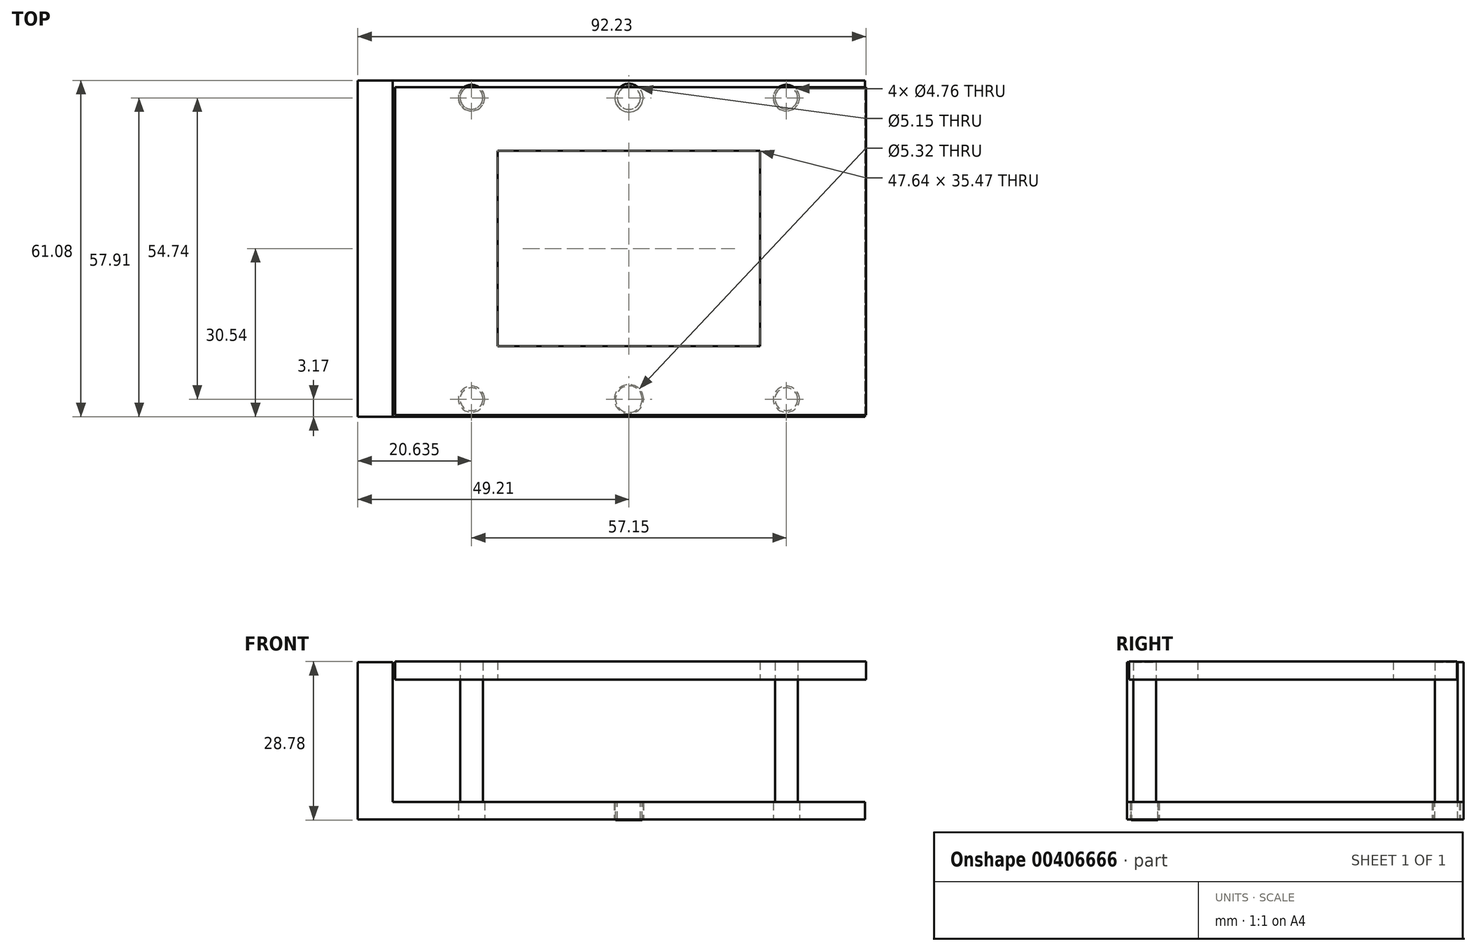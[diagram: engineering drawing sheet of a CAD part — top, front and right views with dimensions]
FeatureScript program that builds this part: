
annotation { "Feature Type Name" : "Feature", "Feature Type Description" : "" }
export const myFeature = defineFeature(function(context is Context, id is Id, definition is map)
    precondition{}
    {
        {
            var Q0;
            Q0=qCreatedBy(makeId("Top.planeOp"),FACE);
            var sketch = newSketch(context, id + "F0", { "sketchPlane" : qUnion([Q0])});
            skLineSegment(sketch, "E0.bottom", {"start": v(42.86, -24.2) * mm, "end": v(-42.86, -24.2) * mm});
            skLineSegment(sketch, "E0.top", {"start": v(42.86, 24.2) * mm, "end": v(-42.86, 24.2) * mm});
            skLineSegment(sketch, "E0.left", {"start": v(42.86, -24.2) * mm, "end": v(42.86, 24.2) * mm});
            skLineSegment(sketch, "E0.right", {"start": v(-42.86, -24.2) * mm, "end": v(-42.86, 24.2) * mm});
            skPoint(sketch, "E0.middle", {"position": v(0, 0) * mm});
            skPoint(sketch, "E1.startSnap0", {"position": v(0, -24.2) * mm});
            skPoint(sketch, "E2.left.start.orphan", {"position": v(49.21, -34.93) * mm});
            skPoint(sketch, "E2.top.start.orphan", {"position": v(49.21, 34.93) * mm});
            skPoint(sketch, "E2.right.end.orphan", {"position": v(-49.21, 34.93) * mm});
            skPoint(sketch, "E2.right.start.orphan", {"position": v(-49.21, -34.93) * mm});
            skCircle(sketch, "E3", {"center": v(28.57, 27.37) * mm, "radius": 2.38 * mm});
            skCircle(sketch, "E4", {"center": v(-28.58, 27.37) * mm, "radius": 2.38 * mm});
            skPoint(sketch, "E5.end.orphan", {"position": v(-37.08, 27.37) * mm});
            skCircle(sketch, "E6", {"center": v(-28.58, -27.37) * mm, "radius": 2.38 * mm});
            skPoint(sketch, "E7.start.orphan", {"position": v(-35.98, -24.2) * mm});
            skPoint(sketch, "E8.orphan", {"position": v(-35.98, -27.37) * mm});
            skPoint(sketch, "E9.orphan", {"position": v(-23.88, -27.37) * mm});
            skPoint(sketch, "E10.start.orphan", {"position": v(0, -12.55) * mm});
            skPoint(sketch, "E11.start.orphan", {"position": v(0, 16.89) * mm});
            skPoint(sketch, "E12.start.orphan", {"position": v(0, -17.21) * mm});
            skPoint(sketch, "E1.start.orphan", {"position": v(0, 12.3) * mm});
            skLineSegment(sketch, "E13", {"start": v(0, -24.2) * mm, "end": v(0, -30.54) * mm});
            skLineSegment(sketch, "E14", {"start": v(42.86, -24.2) * mm, "end": v(42.86, -30.54) * mm});
            skLineSegment(sketch, "E15", {"start": v(-42.86, -24.2) * mm, "end": v(-42.86, -30.54) * mm});
            skLineSegment(sketch, "E16", {"start": v(0, -30.54) * mm, "end": v(42.86, -30.54) * mm});
            skLineSegment(sketch, "E17", {"start": v(-42.86, -30.54) * mm, "end": v(0, -30.54) * mm});
            skLineSegment(sketch, "E18", {"start": v(-42.86, 0) * mm, "end": v(-49.21, 0) * mm});
            skPoint(sketch, "E18.endSnap0", {"position": v(-42.86, 0) * mm});
            skLineSegment(sketch, "E19", {"start": v(-49.21, 0) * mm, "end": v(-49.21, -30.54) * mm});
            skLineSegment(sketch, "E20", {"start": v(-49.21, 0) * mm, "end": v(-49.21, 30.54) * mm});
            skLineSegment(sketch, "E21", {"start": v(-42.86, -30.54) * mm, "end": v(-49.21, -30.54) * mm});
            skPoint(sketch, "E22.endSnap0", {"position": v(0, 24.2) * mm});
            skLineSegment(sketch, "E23", {"start": v(42.86, 24.2) * mm, "end": v(42.86, 30.54) * mm});
            skLineSegment(sketch, "E24", {"start": v(0, 30.54) * mm, "end": v(42.86, 30.54) * mm});
            skLineSegment(sketch, "E25", {"start": v(0, 30.54) * mm, "end": v(-49.21, 30.54) * mm});
            skPoint(sketch, "E22.start.orphan", {"position": v(0, 24.2) * mm});
            skLineSegment(sketch, "E26", {"start": v(28.57, 27.37) * mm, "end": v(28.57, 3.32) * mm});
            skCircle(sketch, "E27", {"center": v(28.57, -27.37) * mm, "radius": 2.38 * mm});
            skLineSegment(sketch, "E28.bottom", {"start": v(4.2, -30.54) * mm, "end": v(-4.2, -30.54) * mm});
            skLineSegment(sketch, "E28.top", {"start": v(4.2, -24.2) * mm, "end": v(-4.2, -24.2) * mm});
            skPoint(sketch, "E28.middle", {"position": v(0, -27.37) * mm});
            skCircle(sketch, "E29", {"center": v(0, -27.37) * mm, "radius": 2.66 * mm});
            skCircle(sketch, "E30", {"center": v(0, 27.37) * mm, "radius": 2.57 * mm});
            skSolve(sketch);
        }
        {
            var Q0;
            Q0 = qSketchRegion(id + "F0", true);
            var Q1;
            {var subQ1=sQuery(id+"F0.wireOp",EDGE,"E15");Q1=makeQuery(id+"F0.imprint","IMPRINT",FACE,{"disambiguationData":[TD([[makeQuery(id+"F0.imprint","IMPRINT",EDGE,{"derivedFrom":subQ1}),-1.0]])]});}
            extrude(context, id + "F1", {"entities" : qUnion([Q0, Q1]), "depth" : 3.17 * mm, "offsetDistance" : 25.4 * mm});
        }
        {
            var Q0;
            Q0=makeQuery(id+"F1.opExtrude","CAP_FACE",FACE,{"disambiguationData":[OSD([sQuery(id+"F0.wireOp",EDGE,"E0.left"),sQuery(id+"F0.wireOp",EDGE,"E3"),sQuery(id+"F0.wireOp",EDGE,"E4"),sQuery(id+"F0.wireOp",EDGE,"E6"),sQuery(id+"F0.wireOp",EDGE,"E14"),sQuery(id+"F0.wireOp",EDGE,"E16"),sQuery(id+"F0.wireOp",EDGE,"E17"),sQuery(id+"F0.wireOp",EDGE,"E19"),sQuery(id+"F0.wireOp",EDGE,"E20"),sQuery(id+"F0.wireOp",EDGE,"E21"),sQuery(id+"F0.wireOp",EDGE,"E23"),sQuery(id+"F0.wireOp",EDGE,"E24"),sQuery(id+"F0.wireOp",EDGE,"E25"),sQuery(id+"F0.wireOp",EDGE,"E27"),sQuery(id+"F0.wireOp",EDGE,"E28.bottom"),sQuery(id+"F0.wireOp",EDGE,"E29"),sQuery(id+"F0.wireOp",EDGE,"E30")])],"isStart":false});
            var sketch = newSketch(context, id + "F2", { "sketchPlane" : qUnion([Q0])});
            skCircle(sketch, "E31", {"center": v(-28.58, 27.37) * mm, "radius": 2.06 * mm});
            skSolve(sketch);
        }
        {
            var Q0;
            Q0 = qSketchRegion(id + "F2", true);
            extrude(context, id + "F3", {"entities" : qUnion([Q0]), "depth" : 25.4 * mm, "offsetDistance" : 25.4 * mm});
        }
        {
            var Q0;
            Q0=makeQuery(id+"F1.opExtrude","CAP_FACE",FACE,{"disambiguationData":[OSD([sQuery(id+"F0.wireOp",EDGE,"E0.left"),sQuery(id+"F0.wireOp",EDGE,"E3"),sQuery(id+"F0.wireOp",EDGE,"E4"),sQuery(id+"F0.wireOp",EDGE,"E6"),sQuery(id+"F0.wireOp",EDGE,"E14"),sQuery(id+"F0.wireOp",EDGE,"E16"),sQuery(id+"F0.wireOp",EDGE,"E17"),sQuery(id+"F0.wireOp",EDGE,"E19"),sQuery(id+"F0.wireOp",EDGE,"E20"),sQuery(id+"F0.wireOp",EDGE,"E21"),sQuery(id+"F0.wireOp",EDGE,"E23"),sQuery(id+"F0.wireOp",EDGE,"E24"),sQuery(id+"F0.wireOp",EDGE,"E25"),sQuery(id+"F0.wireOp",EDGE,"E27"),sQuery(id+"F0.wireOp",EDGE,"E28.bottom"),sQuery(id+"F0.wireOp",EDGE,"E29"),sQuery(id+"F0.wireOp",EDGE,"E30")])],"isStart":false});
            var sketch = newSketch(context, id + "F4", { "sketchPlane" : qUnion([Q0])});
            skCircle(sketch, "E32", {"center": v(28.57, 27.37) * mm, "radius": 2.05 * mm});
            skSolve(sketch);
        }
        {
            var Q0;
            Q0 = qSketchRegion(id + "F4", true);
            extrude(context, id + "F5", {"entities" : qUnion([Q0]), "depth" : 25.4 * mm, "offsetDistance" : 25.4 * mm});
        }
        {
            var Q0;
            Q0=makeQuery(id+"F1.opExtrude","CAP_FACE",FACE,{"disambiguationData":[OSD([sQuery(id+"F0.wireOp",EDGE,"E0.left"),sQuery(id+"F0.wireOp",EDGE,"E3"),sQuery(id+"F0.wireOp",EDGE,"E4"),sQuery(id+"F0.wireOp",EDGE,"E6"),sQuery(id+"F0.wireOp",EDGE,"E14"),sQuery(id+"F0.wireOp",EDGE,"E16"),sQuery(id+"F0.wireOp",EDGE,"E17"),sQuery(id+"F0.wireOp",EDGE,"E19"),sQuery(id+"F0.wireOp",EDGE,"E20"),sQuery(id+"F0.wireOp",EDGE,"E21"),sQuery(id+"F0.wireOp",EDGE,"E23"),sQuery(id+"F0.wireOp",EDGE,"E24"),sQuery(id+"F0.wireOp",EDGE,"E25"),sQuery(id+"F0.wireOp",EDGE,"E27"),sQuery(id+"F0.wireOp",EDGE,"E28.bottom"),sQuery(id+"F0.wireOp",EDGE,"E29"),sQuery(id+"F0.wireOp",EDGE,"E30")])],"isStart":false});
            var sketch = newSketch(context, id + "F6", { "sketchPlane" : qUnion([Q0])});
            skCircle(sketch, "E33", {"center": v(-28.58, -27.37) * mm, "radius": 2.07 * mm});
            skSolve(sketch);
        }
        {
            var Q0;
            Q0 = qSketchRegion(id + "F6", true);
            extrude(context, id + "F7", {"entities" : qUnion([Q0]), "depth" : 25.4 * mm, "offsetDistance" : 25.4 * mm});
        }
        {
            var Q0;
            Q0=makeQuery(id+"F1.opExtrude","CAP_FACE",FACE,{"disambiguationData":[OSD([sQuery(id+"F0.wireOp",EDGE,"E0.left"),sQuery(id+"F0.wireOp",EDGE,"E3"),sQuery(id+"F0.wireOp",EDGE,"E4"),sQuery(id+"F0.wireOp",EDGE,"E6"),sQuery(id+"F0.wireOp",EDGE,"E14"),sQuery(id+"F0.wireOp",EDGE,"E16"),sQuery(id+"F0.wireOp",EDGE,"E17"),sQuery(id+"F0.wireOp",EDGE,"E19"),sQuery(id+"F0.wireOp",EDGE,"E20"),sQuery(id+"F0.wireOp",EDGE,"E21"),sQuery(id+"F0.wireOp",EDGE,"E23"),sQuery(id+"F0.wireOp",EDGE,"E24"),sQuery(id+"F0.wireOp",EDGE,"E25"),sQuery(id+"F0.wireOp",EDGE,"E27"),sQuery(id+"F0.wireOp",EDGE,"E28.bottom"),sQuery(id+"F0.wireOp",EDGE,"E29"),sQuery(id+"F0.wireOp",EDGE,"E30")])],"isStart":false});
            var sketch = newSketch(context, id + "F8", { "sketchPlane" : qUnion([Q0])});
            skCircle(sketch, "E34", {"center": v(28.57, -27.37) * mm, "radius": 2.06 * mm});
            skSolve(sketch);
        }
        {
            var Q0;
            Q0 = qSketchRegion(id + "F8", true);
            extrude(context, id + "F9", {"entities" : qUnion([Q0]), "depth" : 25.4 * mm, "offsetDistance" : 25.4 * mm});
        }
        {
            var Q0;
            Q0=makeQuery(id+"F1.opExtrude","CAP_FACE",FACE,{"disambiguationData":[OSD([sQuery(id+"F0.wireOp",EDGE,"E0.left"),sQuery(id+"F0.wireOp",EDGE,"E3"),sQuery(id+"F0.wireOp",EDGE,"E4"),sQuery(id+"F0.wireOp",EDGE,"E6"),sQuery(id+"F0.wireOp",EDGE,"E14"),sQuery(id+"F0.wireOp",EDGE,"E16"),sQuery(id+"F0.wireOp",EDGE,"E17"),sQuery(id+"F0.wireOp",EDGE,"E19"),sQuery(id+"F0.wireOp",EDGE,"E20"),sQuery(id+"F0.wireOp",EDGE,"E21"),sQuery(id+"F0.wireOp",EDGE,"E23"),sQuery(id+"F0.wireOp",EDGE,"E24"),sQuery(id+"F0.wireOp",EDGE,"E25"),sQuery(id+"F0.wireOp",EDGE,"E27"),sQuery(id+"F0.wireOp",EDGE,"E28.bottom"),sQuery(id+"F0.wireOp",EDGE,"E29"),sQuery(id+"F0.wireOp",EDGE,"E30")])],"isStart":false});
            var sketch = newSketch(context, id + "F10", { "sketchPlane" : qUnion([Q0])});
            skCircle(sketch, "E35", {"center": v(0, 27.37) * mm, "radius": 2.09 * mm});
            skSolve(sketch);
        }
        {
            var Q0;
            Q0 = qSketchRegion(id + "F10", true);
            extrude(context, id + "F11", {"entities" : qUnion([Q0]), "oppositeDirection" : true, "depth" : 3.17 * mm, "offsetDistance" : 25.4 * mm});
        }
        {
            var Q0;
            Q0=makeQuery(id+"F1.opExtrude","CAP_FACE",FACE,{"disambiguationData":[OSD([sQuery(id+"F0.wireOp",EDGE,"E0.left"),sQuery(id+"F0.wireOp",EDGE,"E3"),sQuery(id+"F0.wireOp",EDGE,"E4"),sQuery(id+"F0.wireOp",EDGE,"E6"),sQuery(id+"F0.wireOp",EDGE,"E14"),sQuery(id+"F0.wireOp",EDGE,"E16"),sQuery(id+"F0.wireOp",EDGE,"E17"),sQuery(id+"F0.wireOp",EDGE,"E19"),sQuery(id+"F0.wireOp",EDGE,"E20"),sQuery(id+"F0.wireOp",EDGE,"E21"),sQuery(id+"F0.wireOp",EDGE,"E23"),sQuery(id+"F0.wireOp",EDGE,"E24"),sQuery(id+"F0.wireOp",EDGE,"E25"),sQuery(id+"F0.wireOp",EDGE,"E27"),sQuery(id+"F0.wireOp",EDGE,"E28.bottom"),sQuery(id+"F0.wireOp",EDGE,"E29"),sQuery(id+"F0.wireOp",EDGE,"E30")])],"isStart":false});
            var sketch = newSketch(context, id + "F12", { "sketchPlane" : qUnion([Q0])});
            skCircle(sketch, "E36", {"center": v(0, -27.37) * mm, "radius": 2.4 * mm});
            skSolve(sketch);
        }
        {
            var Q0;
            Q0 = qSketchRegion(id + "F12", true);
            extrude(context, id + "F13", {"entities" : qUnion([Q0]), "oppositeDirection" : true, "depth" : 3.25 * mm, "offsetDistance" : 25.4 * mm});
        }
        {
            var Q0;
            Q0=makeQuery(id+"F1.opExtrude","CAP_FACE",FACE,{"disambiguationData":[OSD([sQuery(id+"F0.wireOp",EDGE,"E0.left"),sQuery(id+"F0.wireOp",EDGE,"E3"),sQuery(id+"F0.wireOp",EDGE,"E4"),sQuery(id+"F0.wireOp",EDGE,"E6"),sQuery(id+"F0.wireOp",EDGE,"E14"),sQuery(id+"F0.wireOp",EDGE,"E16"),sQuery(id+"F0.wireOp",EDGE,"E17"),sQuery(id+"F0.wireOp",EDGE,"E19"),sQuery(id+"F0.wireOp",EDGE,"E20"),sQuery(id+"F0.wireOp",EDGE,"E21"),sQuery(id+"F0.wireOp",EDGE,"E23"),sQuery(id+"F0.wireOp",EDGE,"E24"),sQuery(id+"F0.wireOp",EDGE,"E25"),sQuery(id+"F0.wireOp",EDGE,"E27"),sQuery(id+"F0.wireOp",EDGE,"E28.bottom"),sQuery(id+"F0.wireOp",EDGE,"E29"),sQuery(id+"F0.wireOp",EDGE,"E30")])],"isStart":false});
            var sketch = newSketch(context, id + "F14", { "sketchPlane" : qUnion([Q0])});
            skLineSegment(sketch, "E37.bottom", {"start": v(-49.21, 30.54) * mm, "end": v(-42.86, 30.54) * mm});
            skLineSegment(sketch, "E37.top", {"start": v(-49.21, -30.54) * mm, "end": v(-42.86, -30.54) * mm});
            skLineSegment(sketch, "E37.left", {"start": v(-49.21, 30.54) * mm, "end": v(-49.21, -30.54) * mm});
            skLineSegment(sketch, "E37.right", {"start": v(-42.86, 30.54) * mm, "end": v(-42.86, -30.54) * mm});
            skSolve(sketch);
        }
        {
            var Q0;
            Q0 = qSketchRegion(id + "F14", true);
            extrude(context, id + "F15", {"entities" : qUnion([Q0]), "operationType" : NewBodyOperationType.ADD, "depth" : 25.4 * mm, "offsetDistance" : 25.4 * mm});
        }
        {
            var Q0;
            Q0=qCreatedBy(makeId("Top.planeOp"),FACE);
            cPlane(context, id + "F16", {"entities" : qUnion([Q0]), "cplaneType" : CPlaneType.OFFSET, "offset" : 25.4 * mm, "width" : 152.4 * mm, "height" : 152.4 * mm});
        }
        {
            var Q0;
            Q0=qCreatedBy(id+"F16.planeOp",FACE);
            var sketch = newSketch(context, id + "F17", { "sketchPlane" : qUnion([Q0])});
            skLineSegment(sketch, "E38.bottom", {"start": v(-42.43, 29.31) * mm, "end": v(43.02, 29.31) * mm});
            skLineSegment(sketch, "E38.top", {"start": v(-42.43, -30.22) * mm, "end": v(43.02, -30.22) * mm});
            skLineSegment(sketch, "E38.left", {"start": v(-42.43, 29.31) * mm, "end": v(-42.43, -30.22) * mm});
            skLineSegment(sketch, "E38.right", {"start": v(43.02, 29.31) * mm, "end": v(43.02, -30.22) * mm});
            skLineSegment(sketch, "E39.bottom", {"start": v(23.82, -17.74) * mm, "end": v(-23.82, -17.74) * mm});
            skLineSegment(sketch, "E39.top", {"start": v(23.82, 17.74) * mm, "end": v(-23.82, 17.74) * mm});
            skLineSegment(sketch, "E39.left", {"start": v(23.82, -17.74) * mm, "end": v(23.82, 17.74) * mm});
            skLineSegment(sketch, "E39.right", {"start": v(-23.82, -17.74) * mm, "end": v(-23.82, 17.74) * mm});
            skPoint(sketch, "E39.middle", {"position": v(0, 0) * mm});
            skSolve(sketch);
        }
        {
            var Q0;
            Q0 = qSketchRegion(id + "F17", true);
            extrude(context, id + "F18", {"entities" : qUnion([Q0]), "depth" : 3.3 * mm, "offsetDistance" : 25.4 * mm});
        }
    });
